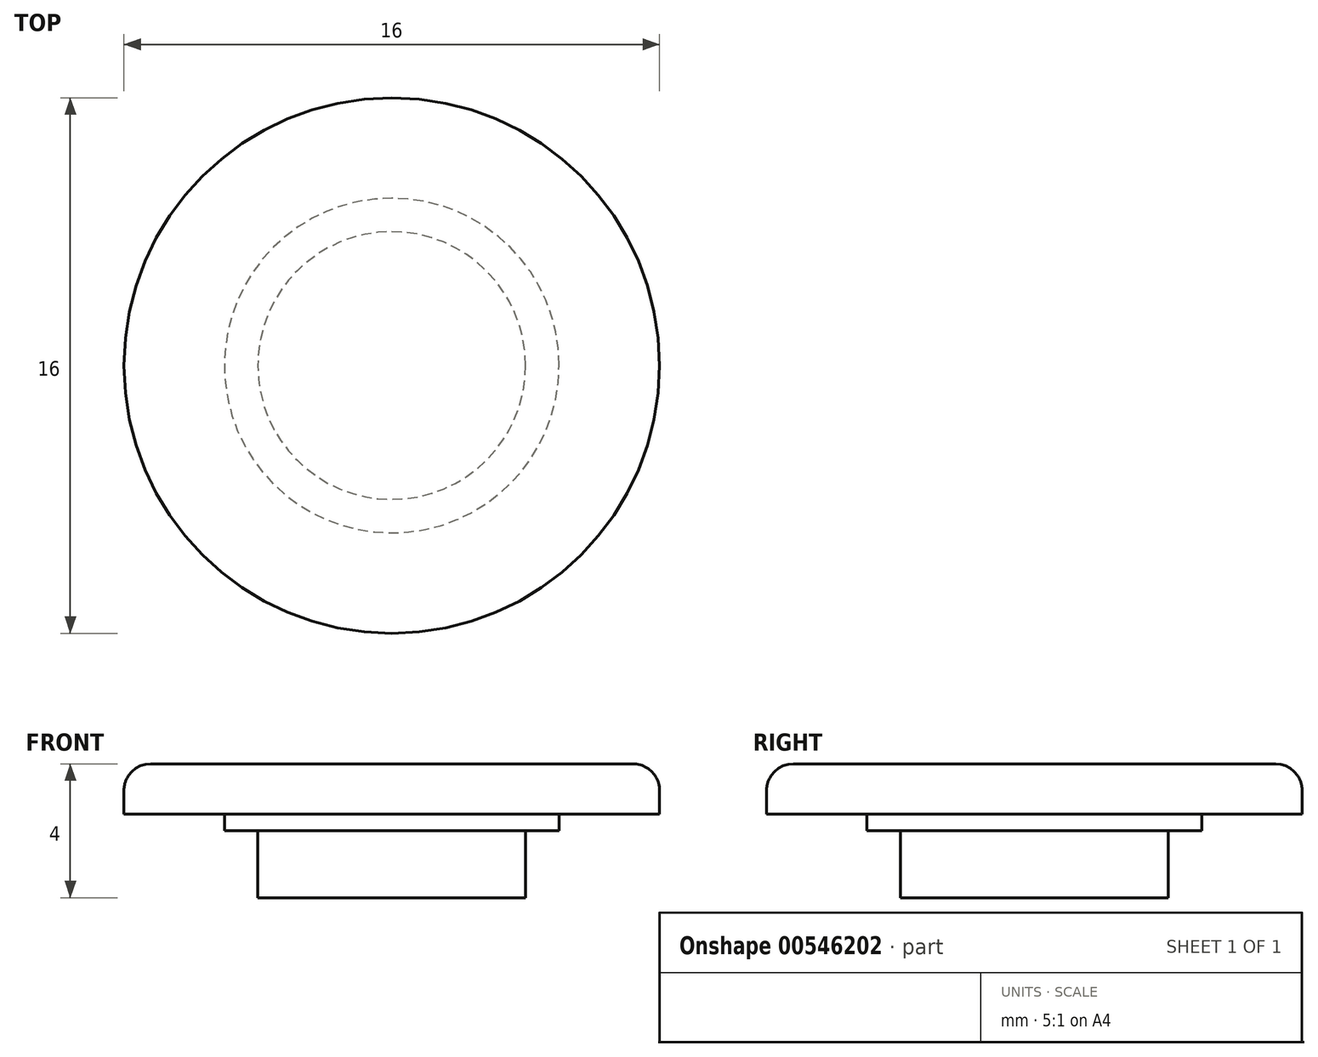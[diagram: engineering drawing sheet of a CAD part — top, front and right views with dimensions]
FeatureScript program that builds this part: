
annotation { "Feature Type Name" : "Feature", "Feature Type Description" : "" }
export const myFeature = defineFeature(function(context is Context, id is Id, definition is map)
    precondition{}
    {
        {
            var Q0;
            Q0=qCreatedBy(makeId("Front.planeOp"),FACE);
            var sketch = newSketch(context, id + "F0", { "sketchPlane" : qUnion([Q0])});
            skLineSegment(sketch, "E0", {"start": v(0, 0) * mm, "end": v(0, 4) * mm, "construction": true});
            skLineSegment(sketch, "E1", {"start": v(0, 4) * mm, "end": v(8, 4) * mm});
            skLineSegment(sketch, "E2", {"start": v(8, 4) * mm, "end": v(8, 2.5) * mm});
            skLineSegment(sketch, "E3", {"start": v(8, 2.5) * mm, "end": v(5, 2.5) * mm});
            skLineSegment(sketch, "E4", {"start": v(5, 2.5) * mm, "end": v(5, 2) * mm});
            skLineSegment(sketch, "E5", {"start": v(5, 2) * mm, "end": v(4, 2) * mm});
            skLineSegment(sketch, "E6", {"start": v(4, 2) * mm, "end": v(4, 0) * mm});
            skLineSegment(sketch, "E7", {"start": v(4, 0) * mm, "end": v(0, 0) * mm});
            skLineSegment(sketch, "E8", {"start": v(0, 4) * mm, "end": v(0, 0) * mm});
            skSolve(sketch);
        }
        {
            var Q0;
            Q0=qSketchRegion(id+"F0",true);
            var Q1;
            Q1=sQuery(id+"F0.wireOp",EDGE,"E8");
            revolve(context, id + "F1", {"entities" : qUnion([Q0]), "axis" : qUnion([Q1]), "revolveType" : RevolveType.FULL});
        }
        {
            var Q0;
            Q0=makeQuery(id+"F1.opRevolve","SWEPT_EDGE",EDGE,{"disambiguationData":[OSD([sQuery(id+"F0.wireOp",EDGE,"E1"),sQuery(id+"F0.wireOp",EDGE,"E2")])]});
            fillet(context, id + "F2", {"entities" : qUnion([Q0]), "radius" : 0.8 * mm, "tangentPropagation" : true, "allowEdgeOverflow" : false});
        }
    });
